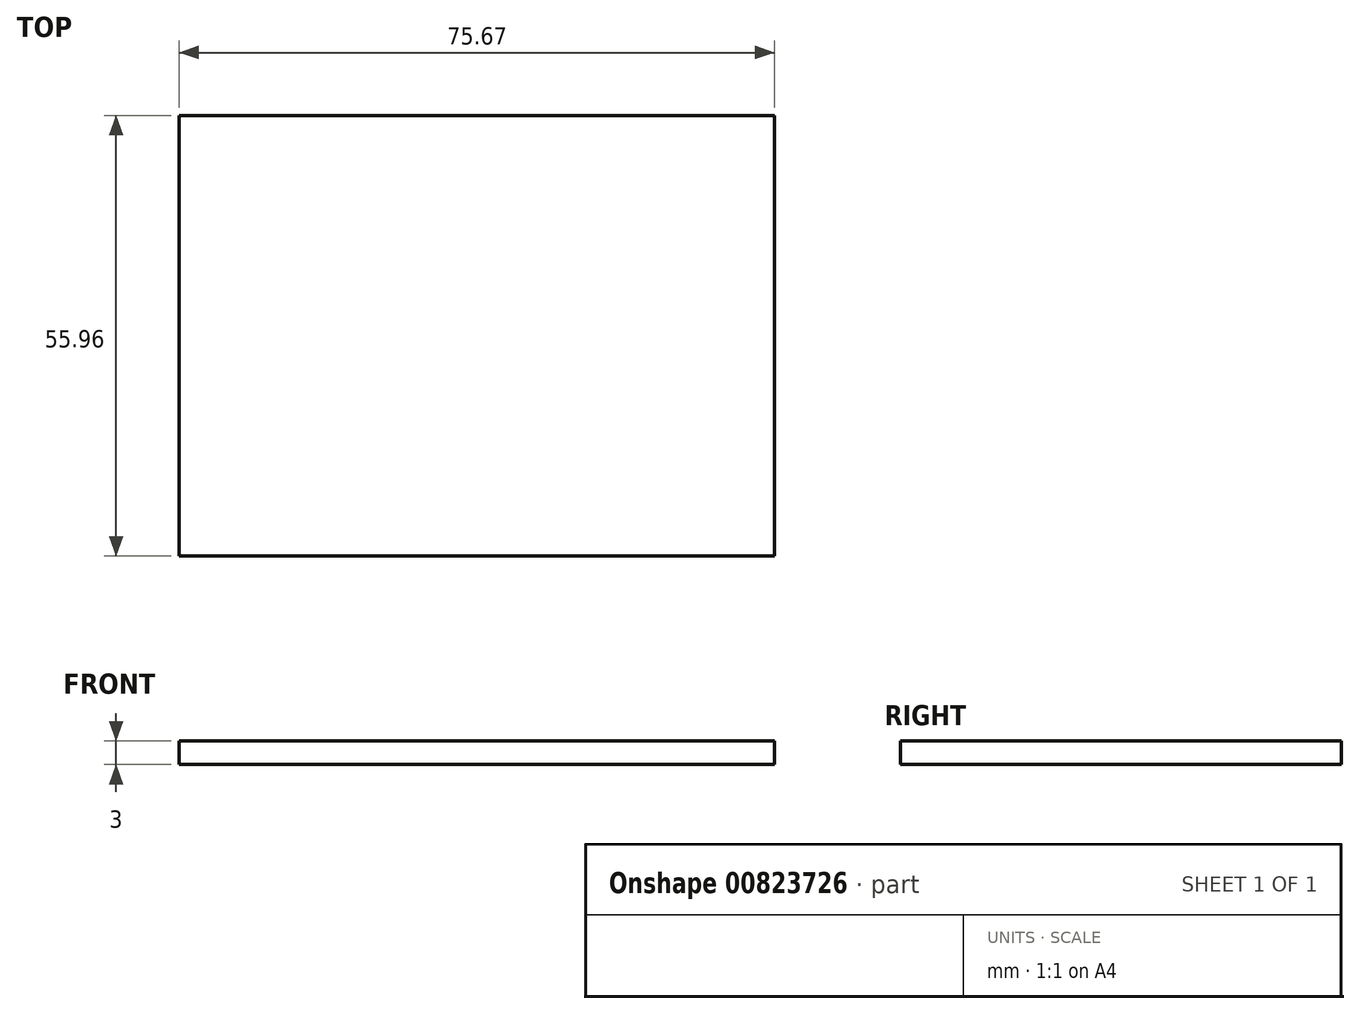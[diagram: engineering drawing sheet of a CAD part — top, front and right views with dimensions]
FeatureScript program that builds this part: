
annotation { "Feature Type Name" : "Feature", "Feature Type Description" : "" }
export const myFeature = defineFeature(function(context is Context, id is Id, definition is map)
    precondition{}
    {
        {
            var Q0;
            Q0=qCreatedBy(makeId("Top.planeOp"),FACE);
            var sketch = newSketch(context, id + "F0", { "sketchPlane" : qUnion([Q0])});
            skLineSegment(sketch, "E0.bottom", {"start": v(0, 0) * mm, "end": v(75.67, 0) * mm});
            skLineSegment(sketch, "E0.top", {"start": v(0, -55.96) * mm, "end": v(75.67, -55.96) * mm});
            skLineSegment(sketch, "E0.left", {"start": v(0, 0) * mm, "end": v(0, -55.96) * mm});
            skLineSegment(sketch, "E0.right", {"start": v(75.67, 0) * mm, "end": v(75.67, -55.96) * mm});
            skSolve(sketch);
        }
        {
            var Q0;
            Q0 = qSketchRegion(id + "F0", true);
            extrude(context, id + "F1", {"entities" : qUnion([Q0]), "depth" : 3 * mm, "offsetDistance" : 25 * mm});
        }
    });
